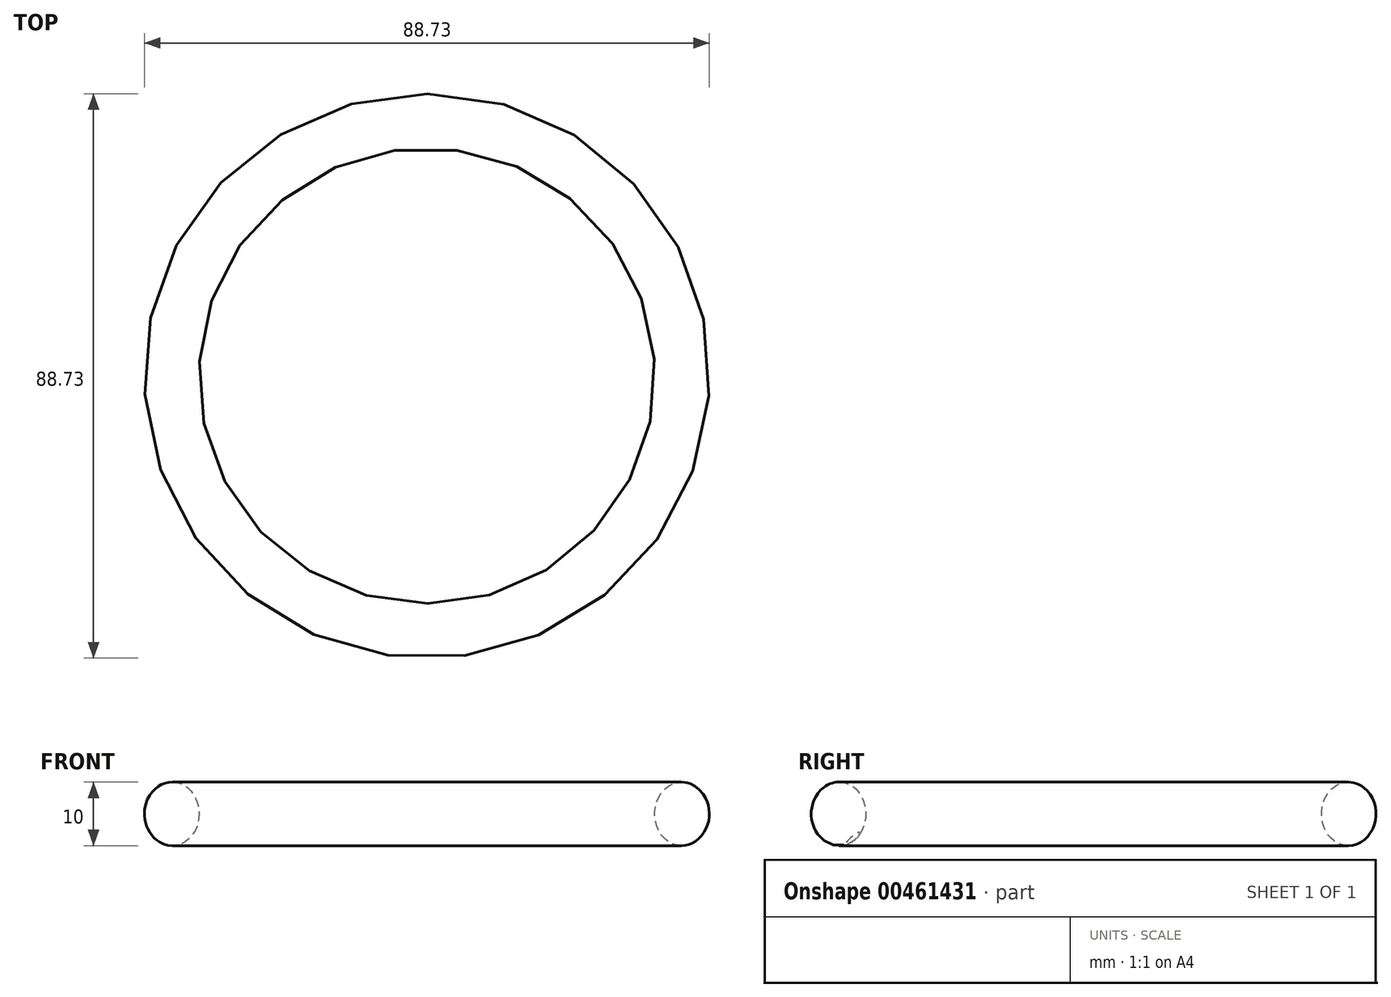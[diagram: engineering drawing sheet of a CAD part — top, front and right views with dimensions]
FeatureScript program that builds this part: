
annotation { "Feature Type Name" : "Feature", "Feature Type Description" : "" }
export const myFeature = defineFeature(function(context is Context, id is Id, definition is map)
    precondition{}
    {
        {
            var Q0;
            Q0=qCreatedBy(makeId("Front.planeOp"),FACE);
            var sketch = newSketch(context, id + "F0", { "sketchPlane" : qUnion([Q0])});
            skCircle(sketch, "E0", {"center": v(0, 0) * mm, "radius": 5 * mm});
            skSolve(sketch);
        }
        {
            var Q0;
            Q0=qCreatedBy(makeId("Top.planeOp"),FACE);
            var sketch = newSketch(context, id + "F1", { "sketchPlane" : qUnion([Q0])});
            skCircle(sketch, "E1", {"center": v(34.34, -20.5) * mm, "radius": 40 * mm});
            skPoint(sketch, "E1.first.point", {"position": v(0, 0) * mm});
            skPoint(sketch, "E1.second.point", {"position": v(68.69, 0) * mm});
            skPoint(sketch, "E1.third.point", {"position": v(72.83, -31.4) * mm});
            skSolve(sketch);
        }
        {
            var Q0;
            Q0=makeQuery(id+"F0.imprint","IMPRINT",FACE,{"disambiguationData":[TD([[makeQuery(id+"F0.imprint","IMPRINT",EDGE,{"derivedFrom":sQuery(id+"F0.wireOp",EDGE,"E0")}),1.0]])]});
            var Q1;
            Q1=sQuery(id+"F1.wireOp",EDGE,"E1");
            revolve(context, id + "F2", {"entities" : qUnion([Q0]), "axis" : qUnion([Q1]), "revolveType" : RevolveType.FULL});
        }
    });
